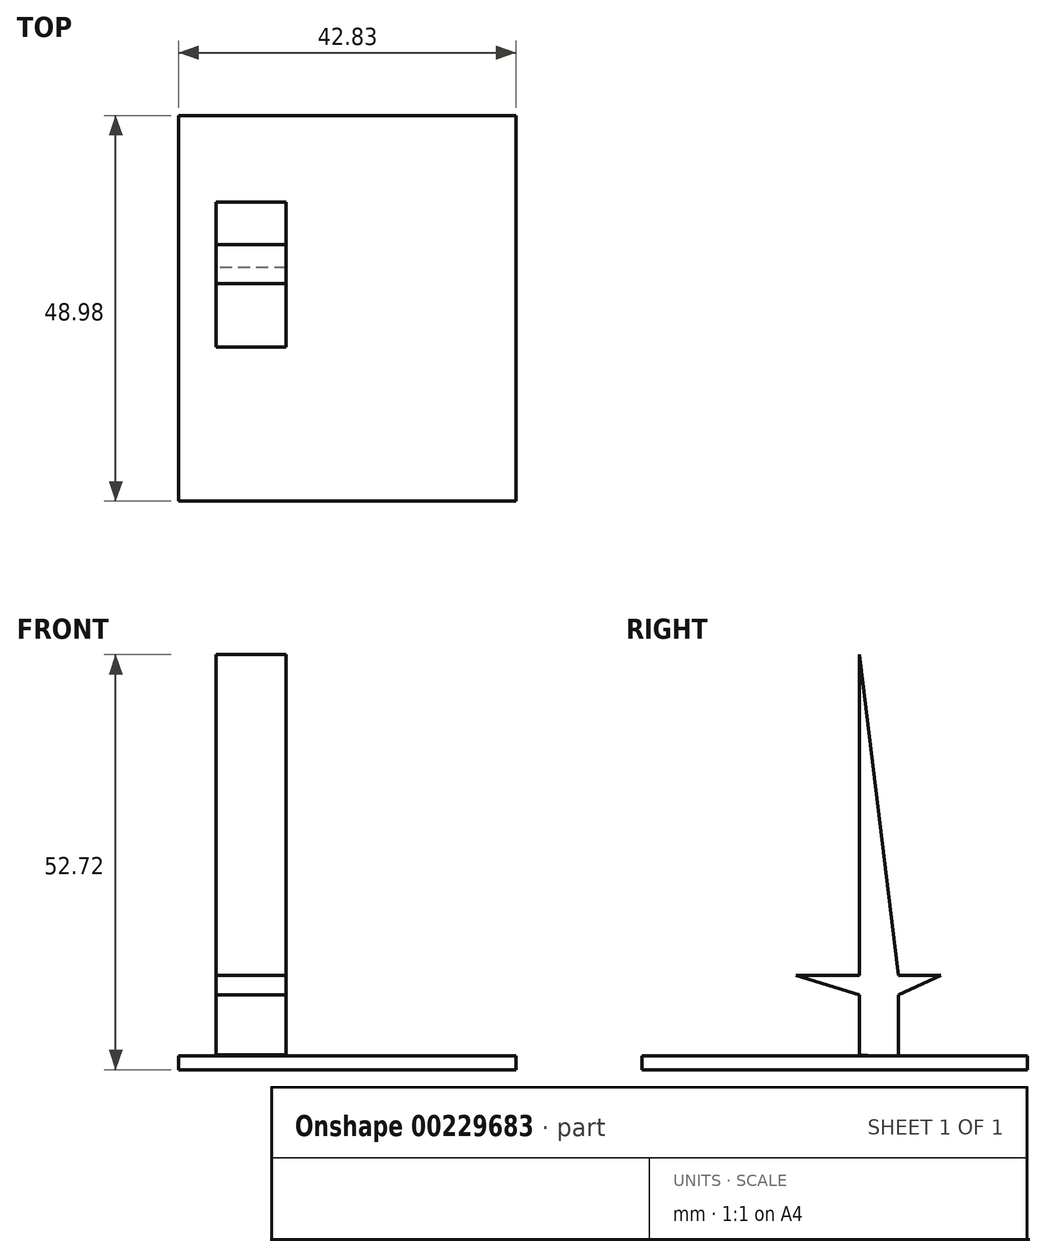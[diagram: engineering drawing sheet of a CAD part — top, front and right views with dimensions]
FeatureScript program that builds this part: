
annotation { "Feature Type Name" : "Feature", "Feature Type Description" : "" }
export const myFeature = defineFeature(function(context is Context, id is Id, definition is map)
    precondition{}
    {
        {
            var Q0;
            Q0=qCreatedBy(makeId("Right.planeOp"),FACE);
            var sketch = newSketch(context, id + "F0", { "sketchPlane" : qUnion([Q0])});
            skLineSegment(sketch, "E0", {"start": v(0, 52.72) * mm, "end": v(4.96, 12) * mm});
            skLineSegment(sketch, "E1", {"start": v(0, 52.72) * mm, "end": v(0, 12) * mm});
            skLineSegment(sketch, "E2", {"start": v(4.96, 12) * mm, "end": v(0, 12) * mm});
            skLineSegment(sketch, "E3", {"start": v(4.96, 12) * mm, "end": v(4.96, 1.65) * mm});
            skLineSegment(sketch, "E4", {"start": v(0, 12) * mm, "end": v(0, 1.86) * mm});
            skLineSegment(sketch, "E5", {"start": v(0, 0) * mm, "end": v(-12.2, -26.46) * mm});
            skLineSegment(sketch, "E6", {"start": v(0, 1.86) * mm, "end": v(4.96, 1.65) * mm});
            skLineSegment(sketch, "E7", {"start": v(4.96, 12) * mm, "end": v(10.34, 12) * mm});
            skLineSegment(sketch, "E8", {"start": v(10.34, 12) * mm, "end": v(0, 12) * mm});
            skLineSegment(sketch, "E9", {"start": v(0, 12) * mm, "end": v(-8.06, 12) * mm});
            skLineSegment(sketch, "E10", {"start": v(-8.06, 12) * mm, "end": v(0, 9.51) * mm});
            skLineSegment(sketch, "E11", {"start": v(0, 9.51) * mm, "end": v(4.96, 9.51) * mm});
            skLineSegment(sketch, "E12", {"start": v(4.96, 9.51) * mm, "end": v(10.34, 12) * mm});
            skSolve(sketch);
        }
        {
            var Q0;
            Q0=qCreatedBy(makeId("Top.planeOp"),FACE);
            var sketch = newSketch(context, id + "F1", { "sketchPlane" : qUnion([Q0])});
            skLineSegment(sketch, "E13.bottom", {"start": v(-4.76, 21.32) * mm, "end": v(38.07, 21.32) * mm});
            skLineSegment(sketch, "E13.top", {"start": v(-4.76, -27.66) * mm, "end": v(38.07, -27.66) * mm});
            skLineSegment(sketch, "E13.left", {"start": v(-4.76, 21.32) * mm, "end": v(-4.76, -27.66) * mm});
            skLineSegment(sketch, "E13.right", {"start": v(38.07, 21.32) * mm, "end": v(38.07, -27.66) * mm});
            skSolve(sketch);
        }
        {
            var Q0;
            Q0 = qSketchRegion(id + "F1", true);
            extrude(context, id + "F2", {"entities" : qUnion([Q0]), "depth" : 1.78 * mm});
        }
        {
            var Q0;
            Q0 = qSketchRegion(id + "F0", true);
            extrude(context, id + "F3", {"entities" : qUnion([Q0]), "operationType" : NewBodyOperationType.ADD, "depth" : 8.9 * mm});
        }
    });
